# Revit family: STC_A3-M-Concrete-Round-Column
name_source: partatom
category: Structural Columns
revit_build: Autodesk Revit 2016 (Build: 20150220_1215(x64)
units: mm (PartAtom-declared; Revit-internal decimal feet)

## family parameters
Always export as geometry = No
Beam cutback in plan = From geometry
Cut with Voids When Loaded = No
Display in Hidden Views = Edges Hidden by Other Members
Material for Model Behavior = Concrete
Section Shape = Not Defined
Shared = No
Show family pre-cut in plan views = Yes

## types (4) — shared parameters

## per-type parameters (varying)
| type | b |
| 300mm Concrete Column | 300 mm |
| 450mm Concrete Column | 450 mm  [stored 1.47638 ft] |
| 600mm Concrete Column | 600 mm |
| 750mm Concrete Column | 750 mm  [stored 2.46063 ft] |

note: [stored X ft] marks values corroborated as IEEE doubles in the binary element streams (Revit-internal decimal feet)

## geometry (parser evidence)
native form markers: Sweep x1
no freeform markers — native parametric forms only
